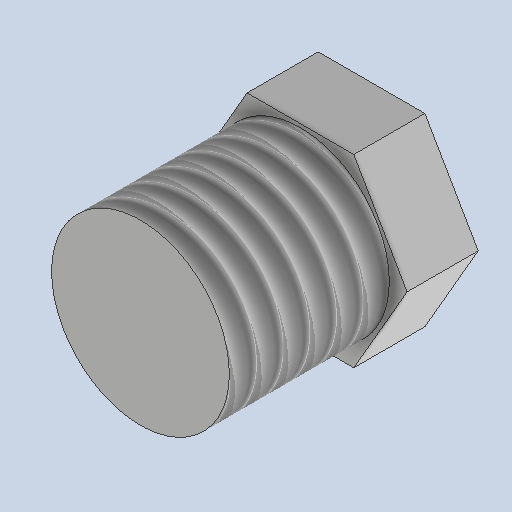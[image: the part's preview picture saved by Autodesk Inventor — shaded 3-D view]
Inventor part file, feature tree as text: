
AUTODESK INVENTOR PART (.ipt)
format: ipt  version: 2025.1 (Build 291241000, 241)  size: 147,968 bytes
history: native  units: mm
features: other x3, sketch x2
ambient origin geometry x8: Origin, YZ Plane, XZ Plane, XY Plane, X Axis, Y Axis, Z Axis, Center Point
bodies: Volumenkörper1 (feature_tree)
feature tree (5):
  other  "1157.ipt"
  other  "Volumenkörper1::1157.ipt"
  other  "TaggingFeature1"
  sketch  "Skizze1"  dims[d0=10.0mm]
  sketch  "Skizze2"
